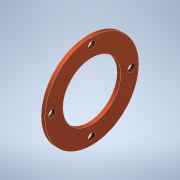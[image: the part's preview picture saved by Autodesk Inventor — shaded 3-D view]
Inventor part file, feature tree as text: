
AUTODESK INVENTOR PART (.ipt)
format: ipt  version: 2021 (Build 250183000, 183)  size: 122,368 bytes
history: native  units: mm
features: extrude x1, sketch x1
ambient origin geometry x8: Origin, YZ Plane, XZ Plane, XY Plane, X Axis, Y Axis, Z Axis, Center Point
bodies: Solid1 (feature_tree)
feature tree (2):
  extrude  "Extrusion1"  Depth=40.0mm
  sketch  "Sketch1"  dims[d1=10.0mm d2=80.0mm d3=130.0mm d4=5.0mm d5=0.0mm d6=40.0mm d8=360.0deg]
